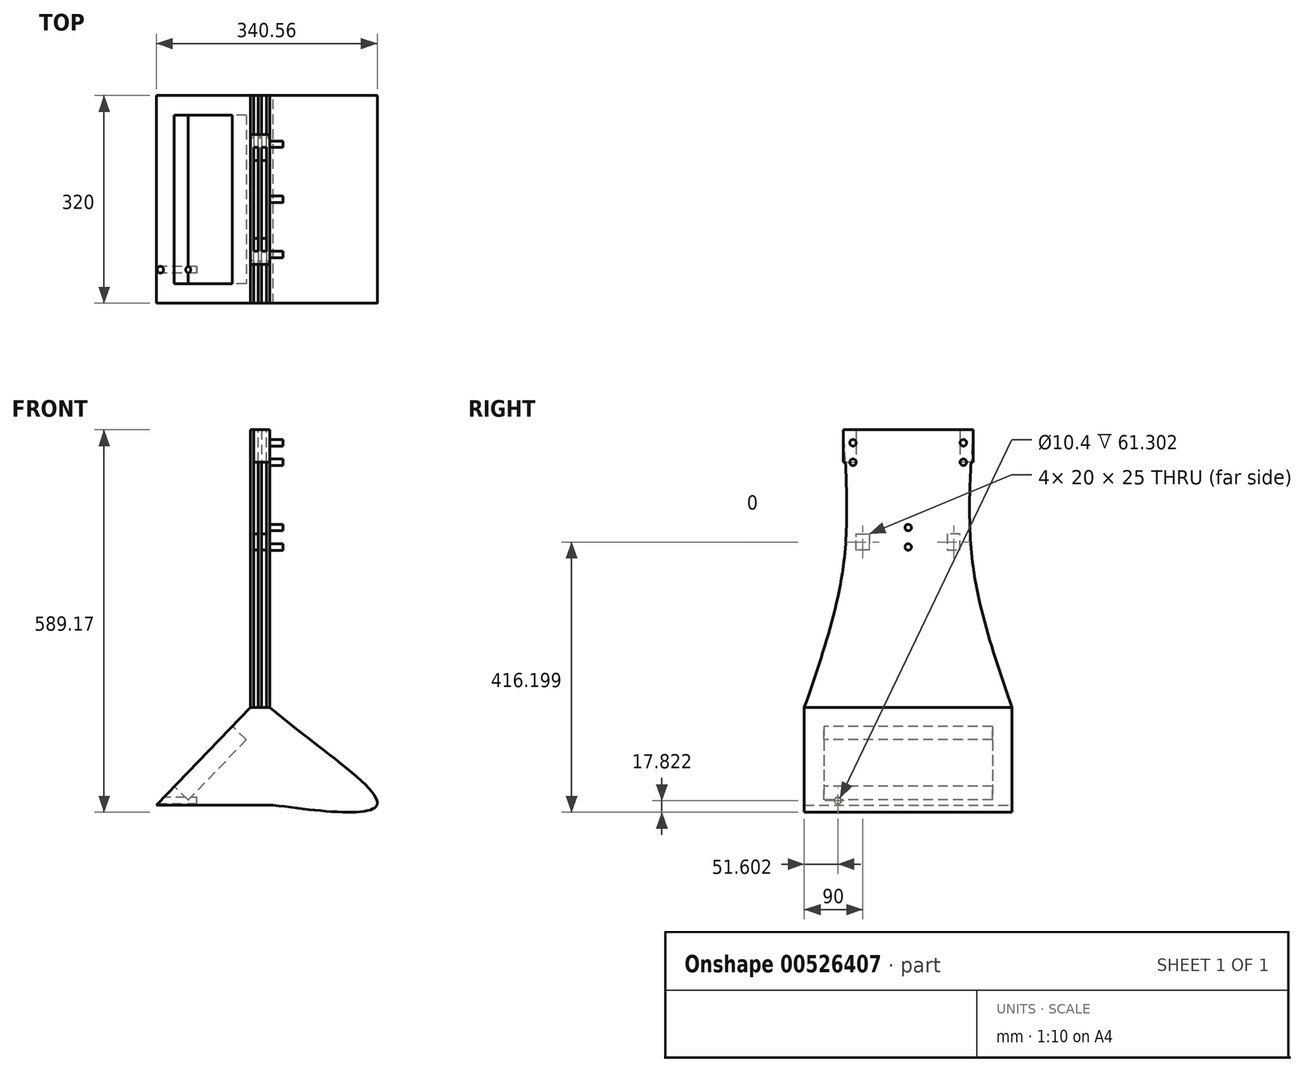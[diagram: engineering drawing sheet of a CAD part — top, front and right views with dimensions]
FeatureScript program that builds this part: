
annotation { "Feature Type Name" : "Feature", "Feature Type Description" : "" }
export const myFeature = defineFeature(function(context is Context, id is Id, definition is map)
    precondition{}
    {
        {
            var Q0;
            Q0=qCreatedBy(makeId("Front.planeOp"),FACE);
            var sketch = newSketch(context, id + "F0", { "sketchPlane" : qUnion([Q0])});
            skFitSpline(sketch, "E0", {"points": [v(180.3, 1.14) * mm, v(340.3, 1.14) * mm, v(175.3, 151.14) * mm], "startDerivative": vector(446.66, -62.32) * mm, "endDerivative": vector(-420, 349.65) * mm});
            skLineSegment(sketch, "E1", {"start": v(180.3, 1.14) * mm, "end": v(340.3, 1.14) * mm});
            skLineSegment(sketch, "E2", {"start": v(175.3, 151.14) * mm, "end": v(145.3, 151.14) * mm});
            skLineSegment(sketch, "E3", {"start": v(150.3, 1.14) * mm, "end": v(180.3, 1.14) * mm});
            skLineSegment(sketch, "E4", {"start": v(150.3, 1.14) * mm, "end": v(100.3, 1.14) * mm});
            skLineSegment(sketch, "E5", {"start": v(100.3, 1.14) * mm, "end": v(0.3, 1.14) * mm});
            skLineSegment(sketch, "E6", {"start": v(0.3, 1.14) * mm, "end": v(145.3, 151.14) * mm});
            skSolve(sketch);
        }
        {
            var Q0;
            Q0 = qSketchRegion(id + "F0", true);
            extrude(context, id + "F1", {"entities" : qUnion([Q0]), "depth" : 320 * mm, "offsetDistance" : 25 * mm});
        }
        {
            var Q0;
            Q0=makeQuery(id+"F1.opExtrude","SWEPT_FACE",FACE,{"disambiguationData":[OSD([sQuery(id+"F0.wireOp",EDGE,"E2")])]});
            var sketch = newSketch(context, id + "F2", { "sketchPlane" : qUnion([Q0])});
            skLineSegment(sketch, "E7", {"start": v(145.3, 0) * mm, "end": v(175.3, 0) * mm});
            skLineSegment(sketch, "E8", {"start": v(175.3, 0) * mm, "end": v(175.3, -320) * mm});
            skLineSegment(sketch, "E9", {"start": v(175.3, -320) * mm, "end": v(145.3, -320) * mm});
            skLineSegment(sketch, "E10", {"start": v(145.3, -320) * mm, "end": v(145.3, 0) * mm});
            skSolve(sketch);
        }
        {
            var Q0;
            Q0 = qSketchRegion(id + "F2", true);
            extrude(context, id + "F3", {"entities" : qUnion([Q0]), "operationType" : NewBodyOperationType.ADD, "depth" : 428 * mm, "offsetDistance" : 25 * mm});
        }
        {
            var Q0;
            Q0=makeQuery(id+"F3.opExtrude","SWEPT_FACE",FACE,{"disambiguationData":[OSD([sQuery(id+"F2.wireOp",EDGE,"E10")])]});
            var sketch = newSketch(context, id + "F4", { "sketchPlane" : qUnion([Q0])});
            skLineSegment(sketch, "E11", {"start": v(0, 151.14) * mm, "end": v(0, 579.14) * mm});
            skLineSegment(sketch, "E12", {"start": v(0, 579.14) * mm, "end": v(60, 579.14) * mm});
            skLineSegment(sketch, "E13", {"start": v(320, 151.14) * mm, "end": v(320, 579.14) * mm});
            skLineSegment(sketch, "E14", {"start": v(320, 579.14) * mm, "end": v(260, 579.14) * mm});
            skFitSpline(sketch, "E15", {"points": [v(60, 579.14) * mm, v(60, 368.67) * mm, v(0, 151.14) * mm], "startDerivative": vector(28.97, -428.6) * mm, "endDerivative": vector(-147.95, -427.4) * mm});
            skFitSpline(sketch, "E16", {"points": [v(320, 151.14) * mm, v(260, 368.67) * mm, v(260, 579.14) * mm], "startDerivative": vector(-147.95, 427.4) * mm, "endDerivative": vector(28.97, 428.6) * mm});
            skLineSegment(sketch, "E17", {"start": v(60, 368.67) * mm, "end": v(60, 579.14) * mm});
            skLineSegment(sketch, "E18", {"start": v(260, 368.67) * mm, "end": v(260, 579.14) * mm});
            skPoint(sketch, "E19.centerSnap0", {"position": v(160, 579.14) * mm});
            skLineSegment(sketch, "E20", {"start": v(260, 579.14) * mm, "end": v(230, 579.14) * mm});
            skPoint(sketch, "E21.end.orphan", {"position": v(260, 508.95) * mm});
            skPoint(sketch, "E22.centerSnap0", {"position": v(230, 544.14) * mm});
            skPoint(sketch, "E22.centerSnap1", {"position": v(245, 579.14) * mm});
            skPoint(sketch, "E23.orphan", {"position": v(230, 509.14) * mm});
            skLineSegment(sketch, "E24", {"start": v(60, 579.14) * mm, "end": v(90, 579.14) * mm});
            skPoint(sketch, "E25.centerSnap0", {"position": v(75, 579.14) * mm});
            skPoint(sketch, "E19.center.orphan", {"position": v(160, 387.68) * mm});
            skPoint(sketch, "E25.center.orphan", {"position": v(75, 559.14) * mm});
            skPoint(sketch, "E26.center.orphan", {"position": v(75, 529.14) * mm});
            skPoint(sketch, "E27.center.orphan", {"position": v(245, 559.14) * mm});
            skPoint(sketch, "E28.center.orphan", {"position": v(245, 529.14) * mm});
            skPoint(sketch, "E29.center.orphan", {"position": v(160, 357.68) * mm});
            skSolve(sketch);
        }
        {
            var Q0;
            Q0 = qSketchRegion(id + "F4", true);
            extrude(context, id + "F5", {"entities" : qUnion([Q0]), "operationType" : NewBodyOperationType.REMOVE, "oppositeDirection" : true, "depth" : 205 * mm, "offsetDistance" : 25 * mm});
        }
        {
            var Q0;
            Q0=makeQuery(id+"F3.opExtrude","SWEPT_FACE",FACE,{"disambiguationData":[OSD([sQuery(id+"F2.wireOp",EDGE,"E8")])]});
            var sketch = newSketch(context, id + "F6", { "sketchPlane" : qUnion([Q0])});
            skLineSegment(sketch, "E30.bottom", {"start": v(-260, 579.14) * mm, "end": v(-240, 579.14) * mm});
            skLineSegment(sketch, "E30.top", {"start": v(-260, 529.14) * mm, "end": v(-240, 529.14) * mm});
            skLineSegment(sketch, "E30.left", {"start": v(-260, 579.14) * mm, "end": v(-260, 529.14) * mm});
            skLineSegment(sketch, "E30.right", {"start": v(-240, 579.14) * mm, "end": v(-240, 529.14) * mm});
            skLineSegment(sketch, "E31.bottom", {"start": v(-60, 579.14) * mm, "end": v(-80, 579.14) * mm});
            skLineSegment(sketch, "E31.top", {"start": v(-60, 529.14) * mm, "end": v(-80, 529.14) * mm});
            skLineSegment(sketch, "E31.left", {"start": v(-60, 579.14) * mm, "end": v(-60, 529.14) * mm});
            skLineSegment(sketch, "E31.right", {"start": v(-80, 579.14) * mm, "end": v(-80, 529.14) * mm});
            skLineSegment(sketch, "E32.right", {"start": v(-240, 393.67) * mm, "end": v(-240, 418.67) * mm});
            skLineSegment(sketch, "E33.right", {"start": v(-80, 393.67) * mm, "end": v(-80, 418.67) * mm});
            skPoint(sketch, "E32.bottom.end.orphan", {"position": v(-240, 368.67) * mm});
            skPoint(sketch, "E34.orphan", {"position": v(-260, 368.67) * mm});
            skPoint(sketch, "E33.bottom.end.orphan", {"position": v(-80, 368.67) * mm});
            skPoint(sketch, "E33.bottom.start.orphan", {"position": v(-60, 368.67) * mm});
            skLineSegment(sketch, "E35", {"start": v(-240, 418.67) * mm, "end": v(-220, 418.67) * mm});
            skLineSegment(sketch, "E36", {"start": v(-220, 418.67) * mm, "end": v(-220, 393.67) * mm});
            skLineSegment(sketch, "E37", {"start": v(-220, 393.67) * mm, "end": v(-240, 393.67) * mm});
            skPoint(sketch, "E32.left.end.orphan", {"position": v(-260, 418.67) * mm});
            skPoint(sketch, "E38.end.orphan", {"position": v(-260, 393.67) * mm});
            skLineSegment(sketch, "E39", {"start": v(-80, 418.67) * mm, "end": v(-100, 418.67) * mm});
            skLineSegment(sketch, "E40", {"start": v(-100, 418.67) * mm, "end": v(-100, 393.67) * mm});
            skLineSegment(sketch, "E41", {"start": v(-100, 393.67) * mm, "end": v(-80, 393.67) * mm});
            skPoint(sketch, "E33.left.end.orphan", {"position": v(-60, 418.67) * mm});
            skPoint(sketch, "E33.left.start.orphan", {"position": v(-60, 393.67) * mm});
            skSolve(sketch);
        }
        {
            var Q0;
            Q0=makeQuery(id+"F1.opExtrude","SWEPT_FACE",FACE,{"disambiguationData":[OSD([sQuery(id+"F0.wireOp",EDGE,"E6")])]});
            var sketch = newSketch(context, id + "F7", { "sketchPlane" : qUnion([Q0])});
            skLineSegment(sketch, "E42.bottom", {"start": v(30, 169.66) * mm, "end": v(290, 169.66) * mm});
            skLineSegment(sketch, "E42.top", {"start": v(30, 41.03) * mm, "end": v(290, 41.03) * mm});
            skLineSegment(sketch, "E42.left", {"start": v(30, 169.66) * mm, "end": v(30, 41.03) * mm});
            skLineSegment(sketch, "E42.right", {"start": v(290, 169.66) * mm, "end": v(290, 41.03) * mm});
            skSolve(sketch);
        }
        {
            var Q0;
            Q0 = qSketchRegion(id + "F7", true);
            extrude(context, id + "F8", {"entities" : qUnion([Q0]), "operationType" : NewBodyOperationType.REMOVE, "oppositeDirection" : true, "depth" : 30 * mm, "offsetDistance" : 25 * mm});
        }
        {
            var Q0;
            Q0=makeQuery(id+"F3.boolean.opBoolean","MERGE",FACE,{"derivedFrom":[makeQuery(id+"F1.opExtrude","CAP_FACE",FACE,{"disambiguationData":[OSD([sQuery(id+"F0.wireOp",EDGE,"E0"),sQuery(id+"F0.wireOp",EDGE,"E1"),sQuery(id+"F0.wireOp",EDGE,"E2"),sQuery(id+"F0.wireOp",EDGE,"E3"),sQuery(id+"F0.wireOp",EDGE,"E4"),sQuery(id+"F0.wireOp",EDGE,"E5"),sQuery(id+"F0.wireOp",EDGE,"E6")])],"isStart":false}),makeQuery(id+"F3.opExtrude","SWEPT_FACE",FACE,{"disambiguationData":[OSD([sQuery(id+"F2.wireOp",EDGE,"E9")])]})]});
            var sketch = newSketch(context, id + "F9", { "sketchPlane" : qUnion([Q0])});
            skLineSegment(sketch, "E43", {"start": v(145.3, 151.14) * mm, "end": v(175.3, 151.14) * mm});
            skLineSegment(sketch, "E44", {"start": v(150.3, 151.14) * mm, "end": v(157.8, 151.14) * mm});
            skLineSegment(sketch, "E45", {"start": v(170.3, 151.14) * mm, "end": v(162.8, 151.14) * mm});
            skLineSegment(sketch, "E46", {"start": v(150.3, 151.14) * mm, "end": v(150.3, 608.36) * mm});
            skLineSegment(sketch, "E47", {"start": v(150.3, 608.36) * mm, "end": v(157.8, 608.36) * mm});
            skLineSegment(sketch, "E48", {"start": v(157.8, 608.36) * mm, "end": v(157.8, 151.14) * mm});
            skLineSegment(sketch, "E49", {"start": v(162.8, 151.14) * mm, "end": v(162.8, 608.36) * mm});
            skLineSegment(sketch, "E50", {"start": v(162.8, 608.36) * mm, "end": v(170.3, 608.36) * mm});
            skLineSegment(sketch, "E51", {"start": v(170.3, 608.36) * mm, "end": v(170.3, 151.14) * mm});
            skSolve(sketch);
        }
        {
            var Q0;
            Q0 = qSketchRegion(id + "F9", true);
            extrude(context, id + "F10", {"entities" : qUnion([Q0]), "operationType" : NewBodyOperationType.REMOVE, "oppositeDirection" : true, "depth" : 977 * mm, "offsetDistance" : 25 * mm});
        }
        {
            var Q0;
            Q0 = qSketchRegion(id + "F6", true);
            extrude(context, id + "F11", {"entities" : qUnion([Q0]), "operationType" : NewBodyOperationType.ADD, "oppositeDirection" : true, "depth" : 25 * mm, "offsetDistance" : 25 * mm});
        }
        {
            var Q0;
            Q0=qCreatedBy(makeId("Right.planeOp"),FACE);
            var sketch = newSketch(context, id + "F12", { "sketchPlane" : qUnion([Q0])});
            skCircle(sketch, "E52", {"center": v(-268.4, 7.8) * mm, "radius": 5.2 * mm});
            skSolve(sketch);
        }
        {
            var Q0;
            Q0 = qSketchRegion(id + "F12", true);
            extrude(context, id + "F13", {"entities" : qUnion([Q0]), "operationType" : NewBodyOperationType.REMOVE, "depth" : 63 * mm, "offsetDistance" : 25 * mm});
        }
        {
            var Q0;
            Q0=makeQuery(id+"F3.opExtrude","SWEPT_FACE",FACE,{"disambiguationData":[OSD([sQuery(id+"F2.wireOp",EDGE,"E8")])]});
            var sketch = newSketch(context, id + "F14", { "sketchPlane" : qUnion([Q0])});
            skCircle(sketch, "E53", {"center": v(-245, 559.14) * mm, "radius": 5 * mm});
            skPoint(sketch, "E53.centerSnap0", {"position": v(-245, 579.14) * mm});
            skCircle(sketch, "E54", {"center": v(-245, 529.14) * mm, "radius": 5 * mm});
            skPoint(sketch, "E55.start.orphan", {"position": v(-260, 579.14) * mm});
            skPoint(sketch, "E56.start.orphan", {"position": v(-230, 579.14) * mm});
            skCircle(sketch, "E57", {"center": v(-75, 559.14) * mm, "radius": 5 * mm});
            skPoint(sketch, "E57.centerSnap0", {"position": v(-75, 579.14) * mm});
            skCircle(sketch, "E58", {"center": v(-75, 529.14) * mm, "radius": 5 * mm});
            skPoint(sketch, "E59.start.orphan", {"position": v(-60, 579.14) * mm});
            skPoint(sketch, "E60.start.orphan", {"position": v(-90, 579.14) * mm});
            skPoint(sketch, "E61.centerSnap0", {"position": v(-160, 579.14) * mm});
            skCircle(sketch, "E62", {"center": v(-160, 428.54) * mm, "radius": 5 * mm});
            skPoint(sketch, "E61.center.orphan", {"position": v(-160, 458.54) * mm});
            skCircle(sketch, "E63", {"center": v(-160, 398.54) * mm, "radius": 5 * mm});
            skSolve(sketch);
        }
        {
            var Q0;
            Q0 = qSketchRegion(id + "F14", true);
            extrude(context, id + "F15", {"entities" : qUnion([Q0]), "operationType" : NewBodyOperationType.ADD, "depth" : 20 * mm, "offsetDistance" : 25 * mm});
        }
    });
